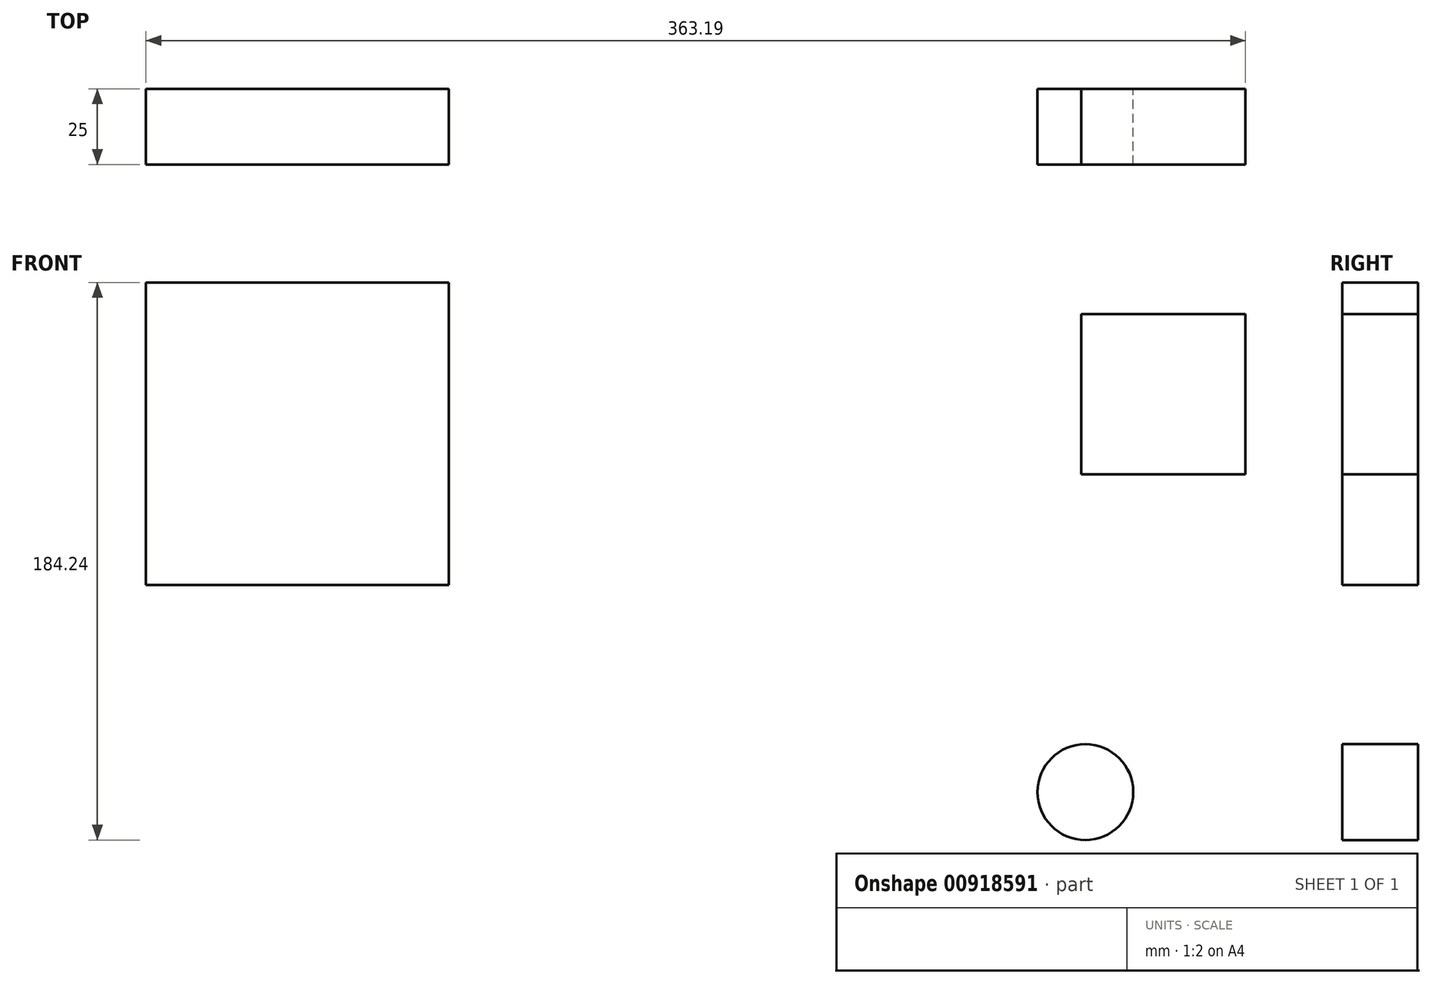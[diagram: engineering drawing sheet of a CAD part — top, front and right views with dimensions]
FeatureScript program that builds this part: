
annotation { "Feature Type Name" : "Feature", "Feature Type Description" : "" }
export const myFeature = defineFeature(function(context is Context, id is Id, definition is map)
    precondition{}
    {
        {
            var Q0;
            Q0=qCreatedBy(makeId("Front.planeOp"),FACE);
            var sketch = newSketch(context, id + "F0", { "sketchPlane" : qUnion([Q0])});
            skLineSegment(sketch, "E0.bottom", {"start": v(-162.92, 62.12) * mm, "end": v(-92.2, 62.12) * mm});
            skLineSegment(sketch, "E0.top", {"start": v(-162.92, -5.72) * mm, "end": v(-92.2, -5.72) * mm});
            skLineSegment(sketch, "E0.left", {"start": v(-162.92, 62.12) * mm, "end": v(-162.92, -5.72) * mm});
            skLineSegment(sketch, "E0.right", {"start": v(-92.2, 62.12) * mm, "end": v(-92.2, -5.72) * mm});
            skSolve(sketch);
        }
        {
            var Q0;
            Q0 = qSketchRegion(id + "F0", true);
            extrude(context, id + "F1", {"entities" : qUnion([Q0]), "depth" : 25 * mm, "offsetDistance" : 25 * mm});
        }
        {
            var Q0;
            Q0=qCreatedBy(makeId("Front.planeOp"),FACE);
            var sketch = newSketch(context, id + "F2", { "sketchPlane" : qUnion([Q0])});
            skLineSegment(sketch, "E1.bottom", {"start": v(-273.17, 100) * mm, "end": v(-173.17, 100) * mm});
            skLineSegment(sketch, "E1.top", {"start": v(-273.17, 0) * mm, "end": v(-173.17, 0) * mm});
            skLineSegment(sketch, "E1.left", {"start": v(-273.17, 100) * mm, "end": v(-273.17, 0) * mm});
            skLineSegment(sketch, "E1.right", {"start": v(-173.17, 100) * mm, "end": v(-173.17, 0) * mm});
            skSolve(sketch);
        }
        {
            var Q0;
            Q0 = qSketchRegion(id + "F2", true);
            extrude(context, id + "F3", {"entities" : qUnion([Q0]), "depth" : 25 * mm, "offsetDistance" : 25 * mm});
        }
        {
            var Q0;
            Q0=qCreatedBy(makeId("Front.planeOp"),FACE);
            var sketch = newSketch(context, id + "F4", { "sketchPlane" : qUnion([Q0])});
            skLineSegment(sketch, "E2.bottom", {"start": v(35.76, 89.61) * mm, "end": v(90.02, 89.61) * mm});
            skLineSegment(sketch, "E2.top", {"start": v(35.76, 36.6) * mm, "end": v(90.02, 36.6) * mm});
            skLineSegment(sketch, "E2.left", {"start": v(35.76, 89.61) * mm, "end": v(35.76, 36.6) * mm});
            skLineSegment(sketch, "E2.right", {"start": v(90.02, 89.61) * mm, "end": v(90.02, 36.6) * mm});
            skSolve(sketch);
        }
        {
            var Q0;
            Q0 = qSketchRegion(id + "F4", true);
            extrude(context, id + "F5", {"entities" : qUnion([Q0]), "depth" : 25 * mm, "offsetDistance" : 25 * mm});
        }
        {
            var Q0;
            Q0=qCreatedBy(makeId("Front.planeOp"),FACE);
            var sketch = newSketch(context, id + "F6", { "sketchPlane" : qUnion([Q0])});
            skCircle(sketch, "E3", {"center": v(37.16, -68.4) * mm, "radius": 15.83 * mm});
            skSolve(sketch);
        }
        {
            var Q0;
            Q0 = qSketchRegion(id + "F6", true);
            extrude(context, id + "F7", {"entities" : qUnion([Q0]), "depth" : 25 * mm, "offsetDistance" : 25 * mm});
        }
        {
            var Q0;
            Q0=makeQuery(id+"F1.opExtrude","SWEPT_BODY",BODY,{"disambiguationData":[OSD([sQuery(id+"F0.wireOp",EDGE,"E0.bottom"),sQuery(id+"F0.wireOp",EDGE,"E0.top"),sQuery(id+"F0.wireOp",EDGE,"E0.left"),sQuery(id+"F0.wireOp",EDGE,"E0.right")])]});
            deleteBodies(context, id + "F8", {"entities" : qUnion([Q0])});
        }
    });
